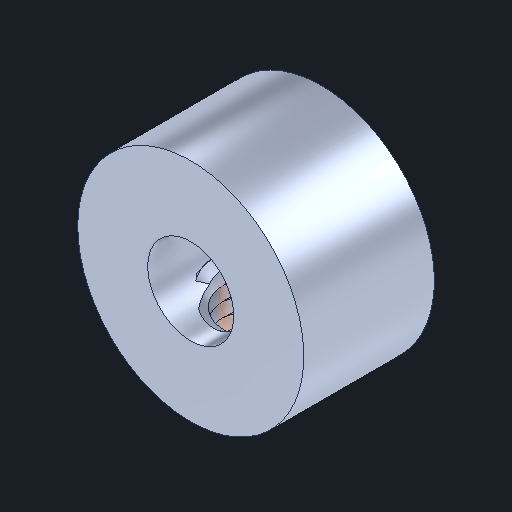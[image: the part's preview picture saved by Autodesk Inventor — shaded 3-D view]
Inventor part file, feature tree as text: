
AUTODESK INVENTOR PART (.ipt)
format: ipt  version: 2024 (Build 280153000, 153)  size: 588,800 bytes
history: native  units: in
note: dims shown in document units (in); Inventor stores cm internally (conversion verified against a paired STEP export)
features: other x6, sketch x3, plane x1
ambient origin geometry x8: Origin, YZ Plane, XZ Plane, XY Plane, X Axis, Y Axis, Z Axis, Center Point
bodies: Body1 (feature_tree), Body2 (feature_tree)
feature tree (10):
  other  "Shaft Collar Metal.ipt"
  other  "NONE::Shaft Collar Metal.ipt"
  other  "TaggingFeature1"
  sketch  "Sketch1"  dims[d0=0.3937in]
  sketch  "Sketch2"
  sketch  "Sketch3"
  plane  "Work Plane1"
  other  "Srf1"
  parser-record x1  (decoder bookkeeping rows leaked as tree rows — omitted from the tree; the rows remain in map.json)
  other  "Srf1::Derived"
